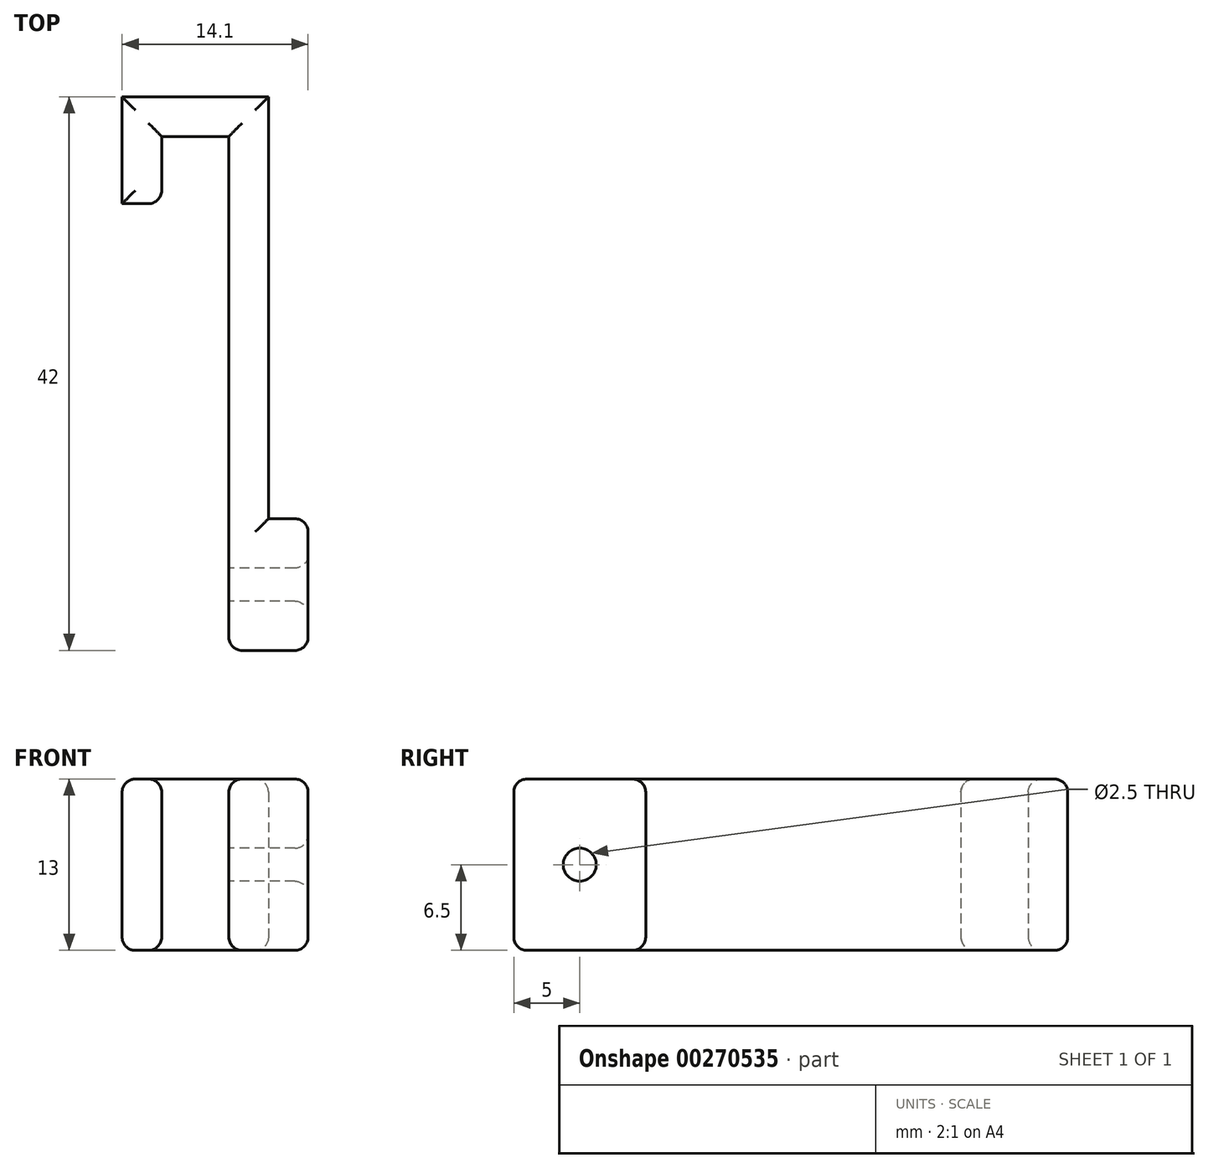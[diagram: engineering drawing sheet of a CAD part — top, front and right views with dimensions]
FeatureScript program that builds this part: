
annotation { "Feature Type Name" : "Feature", "Feature Type Description" : "" }
export const myFeature = defineFeature(function(context is Context, id is Id, definition is map)
    precondition{}
    {
        {
            var Q0;
            Q0=qCreatedBy(makeId("Top.planeOp"),FACE);
            var sketch = newSketch(context, id + "F0", { "sketchPlane" : qUnion([Q0])});
            skLineSegment(sketch, "E0", {"start": v(-8.63, 33.9) * mm, "end": v(-11.63, 33.9) * mm});
            skLineSegment(sketch, "E1", {"start": v(-11.63, 33.9) * mm, "end": v(-11.63, 42) * mm});
            skLineSegment(sketch, "E2", {"start": v(-11.63, 42) * mm, "end": v(-0.53, 42) * mm});
            skLineSegment(sketch, "E3", {"start": v(-0.53, 42) * mm, "end": v(-0.53, 0) * mm});
            skLineSegment(sketch, "E4", {"start": v(-0.53, 0) * mm, "end": v(-3.53, 0) * mm});
            skLineSegment(sketch, "E5", {"start": v(-3.53, 0) * mm, "end": v(-3.53, 39) * mm});
            skLineSegment(sketch, "E6", {"start": v(-3.53, 39) * mm, "end": v(-8.63, 39) * mm});
            skLineSegment(sketch, "E7", {"start": v(-8.63, 39) * mm, "end": v(-8.63, 33.9) * mm});
            skSolve(sketch);
        }
        {
            var Q0;
            Q0 = qSketchRegion(id + "F0", true);
            extrude(context, id + "F1", {"entities" : qUnion([Q0]), "depth" : 13 * mm});
        }
        {
            var Q0;
            Q0=makeQuery(id+"F1.opExtrude","SWEPT_FACE",FACE,{"disambiguationData":[OSD([sQuery(id+"F0.wireOp",EDGE,"E3")])]});
            var sketch = newSketch(context, id + "F2", { "sketchPlane" : qUnion([Q0])});
            skCircle(sketch, "E8", {"center": v(5, 6.5) * mm, "radius": 1.25 * mm});
            skPoint(sketch, "E9", {"position": v(0, 6.5) * mm});
            skLineSegment(sketch, "E10.0", {"start": v(0, 13) * mm, "end": v(0, 0) * mm});
            skLineSegment(sketch, "E10.1", {"start": v(42, 13) * mm, "end": v(0, 13) * mm});
            skLineSegment(sketch, "E10.2", {"start": v(42, 0) * mm, "end": v(0, 0) * mm});
            skLineSegment(sketch, "E11", {"start": v(10, 13) * mm, "end": v(10, 0) * mm});
            skSolve(sketch);
        }
        {
            var Q0;
            Q0 = qSketchRegion(id + "F2", true);
            extrude(context, id + "F3", {"entities" : qUnion([Q0]), "operationType" : NewBodyOperationType.ADD, "depth" : 3 * mm});
        }
        {
            var Q0;
            Q0=makeQuery(id+"F2.imprint","IMPRINT",FACE,{"disambiguationData":[TD([[makeQuery(id+"F2.imprint","IMPRINT",EDGE,{"derivedFrom":sQuery(id+"F2.wireOp",EDGE,"E8")}),1.0]])]});
            extrude(context, id + "F4", {"entities" : qUnion([Q0]), "operationType" : NewBodyOperationType.REMOVE, "oppositeDirection" : true, "depth" : 25 * mm});
        }
        {
            var Q0;
            Q0=makeQuery(id+"F1.opExtrude","SWEPT_EDGE",EDGE,{"disambiguationData":[OSD([sQuery(id+"F0.wireOp",EDGE,"E0"),sQuery(id+"F0.wireOp",EDGE,"E7")])]});
            var Q1;
            Q1=makeQuery(id+"F1.opExtrude","SWEPT_EDGE",EDGE,{"disambiguationData":[OSD([sQuery(id+"F0.wireOp",EDGE,"E4"),sQuery(id+"F0.wireOp",EDGE,"E5")])]});
            var Q2;
            Q2=makeQuery(id+"F3.opExtrude","CAP_EDGE",EDGE,{"disambiguationData":[OSD([sQuery(id+"F2.wireOp",EDGE,"E11")])],"isStart":false});
            var Q3;
            Q3=makeQuery(id+"F3.opExtrude","CAP_EDGE",EDGE,{"disambiguationData":[OSD([sQuery(id+"F2.wireOp",EDGE,"E10.1")])],"isStart":false});
            var Q4;
            Q4=makeQuery(id+"F3.opExtrude","CAP_EDGE",EDGE,{"disambiguationData":[OSD([sQuery(id+"F2.wireOp",EDGE,"E10.0")])],"isStart":false});
            var Q5;
            Q5=makeQuery(id+"F3.opExtrude","CAP_EDGE",EDGE,{"disambiguationData":[OSD([sQuery(id+"F2.wireOp",EDGE,"E10.2")])],"isStart":false});
            var Q6;
            Q6=makeQuery(id+"F3.opExtrude","CAP_EDGE",EDGE,{"disambiguationData":[OSD([sQuery(id+"F2.wireOp",EDGE,"E8")])],"isStart":false});
            var Q7;
            Q7=makeQuery(id+"F1.opExtrude","CAP_EDGE",EDGE,{"disambiguationData":[OSD([sQuery(id+"F0.wireOp",EDGE,"E3")])],"isStart":false});
            var Q8;
            Q8=makeQuery(id+"F3.boolean.opBoolean","MERGE",FACE,{"derivedFrom":[makeQuery(id+"F1.opExtrude","CAP_FACE",FACE,{"disambiguationData":[OSD([sQuery(id+"F0.wireOp",EDGE,"E0"),sQuery(id+"F0.wireOp",EDGE,"E1"),sQuery(id+"F0.wireOp",EDGE,"E2"),sQuery(id+"F0.wireOp",EDGE,"E3"),sQuery(id+"F0.wireOp",EDGE,"E4"),sQuery(id+"F0.wireOp",EDGE,"E5"),sQuery(id+"F0.wireOp",EDGE,"E6"),sQuery(id+"F0.wireOp",EDGE,"E7")])],"isStart":false}),makeQuery(id+"F3.opExtrude","SWEPT_FACE",FACE,{"disambiguationData":[OSD([sQuery(id+"F2.wireOp",EDGE,"E10.1")])]})]});
            var Q9;
            Q9=makeQuery(id+"F3.boolean.opBoolean","MERGE",FACE,{"derivedFrom":[makeQuery(id+"F1.opExtrude","CAP_FACE",FACE,{"disambiguationData":[OSD([sQuery(id+"F0.wireOp",EDGE,"E0"),sQuery(id+"F0.wireOp",EDGE,"E1"),sQuery(id+"F0.wireOp",EDGE,"E2"),sQuery(id+"F0.wireOp",EDGE,"E3"),sQuery(id+"F0.wireOp",EDGE,"E4"),sQuery(id+"F0.wireOp",EDGE,"E5"),sQuery(id+"F0.wireOp",EDGE,"E6"),sQuery(id+"F0.wireOp",EDGE,"E7")])],"isStart":true}),makeQuery(id+"F3.opExtrude","SWEPT_FACE",FACE,{"disambiguationData":[OSD([sQuery(id+"F2.wireOp",EDGE,"E10.2")])]})]});
            fillet(context, id + "F5", {"entities" : qUnion([Q0, Q1, Q2, Q3, Q4, Q5, Q6, Q7, Q8, Q9]), "radius" : 1 * mm, "tangentPropagation" : true, "allowEdgeOverflow" : false});
        }
    });
